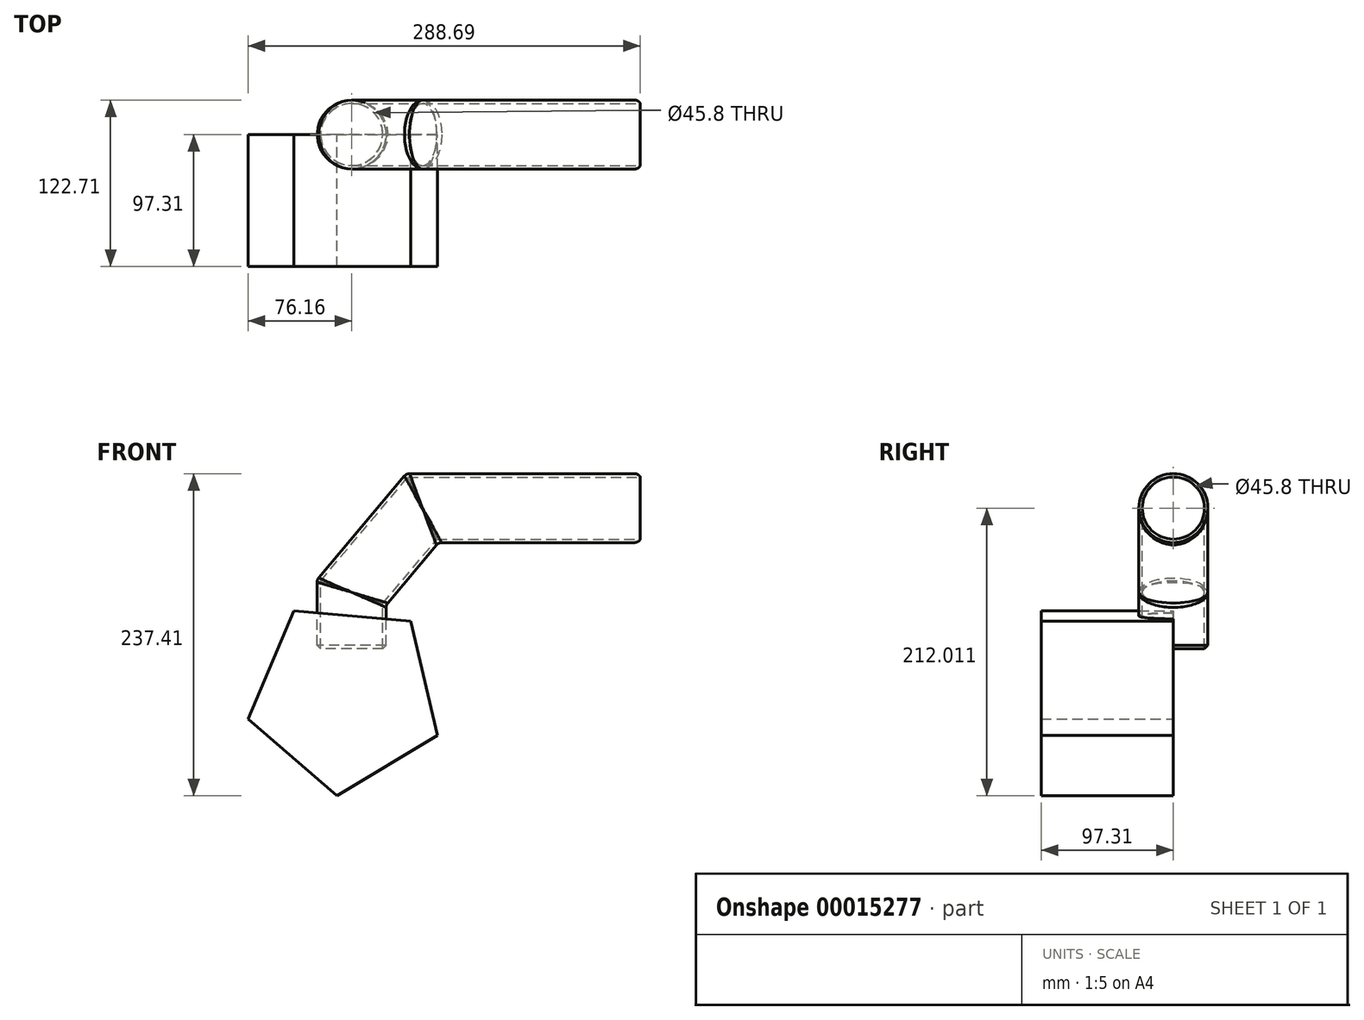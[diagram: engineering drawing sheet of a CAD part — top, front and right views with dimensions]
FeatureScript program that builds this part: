
annotation { "Feature Type Name" : "Feature", "Feature Type Description" : "" }
export const myFeature = defineFeature(function(context is Context, id is Id, definition is map)
    precondition{}
    {
        {
            var Q0;
            Q0=qCreatedBy(makeId("Top.planeOp"),FACE);
            var sketch = newSketch(context, id + "F0", { "sketchPlane" : qUnion([Q0])});
            skCircle(sketch, "E0", {"center": v(0, 0) * mm, "radius": 25.4 * mm});
            skSolve(sketch);
        }
        {
            var Q0;
            Q0=qCreatedBy(makeId("Front.planeOp"),FACE);
            var sketch = newSketch(context, id + "F1", { "sketchPlane" : qUnion([Q0])});
            skLineSegment(sketch, "E1", {"start": v(0, 0) * mm, "end": v(0, 44) * mm});
            skLineSegment(sketch, "E2", {"start": v(0, 44) * mm, "end": v(52.13, 106.03) * mm});
            skLineSegment(sketch, "E3", {"start": v(52.13, 106.03) * mm, "end": v(108.85, 106.03) * mm});
            skSolve(sketch);
        }
        {
            var Q0;
            Q0=makeQuery(id+"F0.imprint","IMPRINT",FACE,{"disambiguationData":[TD([[makeQuery(id+"F0.imprint","IMPRINT",EDGE,{"derivedFrom":sQuery(id+"F0.wireOp",EDGE,"E0")}),1.0]])]});
            var Q1;
            Q1=sQuery(id+"F1.wireOp",EDGE,"E1");
            var Q2;
            Q2=sQuery(id+"F1.wireOp",EDGE,"E2");
            var Q3;
            Q3=sQuery(id+"F1.wireOp",EDGE,"E3");
            sweep(context, id + "F2", {"profiles" : qUnion([Q0]), "path" : qUnion([Q1, Q2, Q3])});
        }
        {
            var Q0;
            Q0=makeQuery(id+"F2.opSweep","CAP_FACE",FACE,{"disambiguationData":[OSD([sQuery(id+"F0.wireOp",EDGE,"E0"),sQuery(id+"F1.wireOp",VERTEX,"E3.end")])],"isStart":false});
            var Q1;
            Q1=makeQuery(id+"F2.opSweep","CAP_FACE",FACE,{"disambiguationData":[OSD([sQuery(id+"F0.wireOp",EDGE,"E0"),sQuery(id+"F1.wireOp",VERTEX,"E1.start")])],"isStart":true});
            shell(context, id + "F3", {"entities" : qUnion([Q0, Q1]), "thickness" : 2.5 * mm});
        }
        {
            var Q0;
            Q0=makeQuery(id+"F2.opSweep","MID_CAP_EDGE",EDGE,{"disambiguationData":[OSD([sQuery(id+"F0.wireOp",EDGE,"E0"),sQuery(id+"F1.wireOp",VERTEX,"E3.start")])],"capPos":2.0});
            var Q1;
            Q1=makeQuery(id+"F2.opSweep","MID_CAP_EDGE",EDGE,{"disambiguationData":[OSD([sQuery(id+"F0.wireOp",EDGE,"E0"),sQuery(id+"F1.wireOp",VERTEX,"E2.start")])],"capPos":1.0});
            fillet(context, id + "F4", {"entities" : qUnion([Q0, Q1]), "radius" : 5 * mm, "tangentPropagation" : true, "allowEdgeOverflow" : false});
        }
        {
            var Q0;
            Q0=makeQuery(id+"F2.opSweep","CAP_EDGE",EDGE,{"disambiguationData":[OSD([sQuery(id+"F0.wireOp",EDGE,"E0"),sQuery(id+"F1.wireOp",VERTEX,"E1.start")])],"isStart":true});
            chamfer(context, id + "F5", {"entities" : qUnion([Q0]), "width" : 5 * mm, "tangentPropagation" : true});
        }
        {
            var Q0;
            Q0=makeQuery(id+"F2.opSweep","CAP_FACE",FACE,{"disambiguationData":[OSD([sQuery(id+"F0.wireOp",EDGE,"E0"),sQuery(id+"F1.wireOp",VERTEX,"E3.end")])],"isStart":false});
            extrude(context, id + "F6", {"entities" : qUnion([Q0]), "operationType" : NewBodyOperationType.ADD, "depth" : 103.68 * mm});
        }
        {
            var Q0;
            {var subQ0=sQuery(id+"F1.wireOp",VERTEX,"E3.end");var subQ1=sQuery(id+"F0.wireOp",EDGE,"E0");Q0=makeQuery(id+"F6.opExtrude","CAP_EDGE",EDGE,{"disambiguationData":[OSD([subQ1,subQ0]),TDD([makeQuery(id+"F2.opSweep","CAP_EDGE",EDGE,{"disambiguationData":[OSD([subQ1,subQ0])],"isStart":false})])],"isStart":false});}
            fillet(context, id + "F7", {"entities" : qUnion([Q0]), "radius" : 5 * mm, "tangentPropagation" : true, "allowEdgeOverflow" : false});
        }
        {
            var Q0;
            Q0=qCreatedBy(makeId("Front.planeOp"),FACE);
            var sketch = newSketch(context, id + "F8", { "sketchPlane" : qUnion([Q0])});
            skCircle(sketch, "E4.cCircle", {"center": v(-4.54, -32.72) * mm, "radius": 59.49 * mm, "construction": true});
            skLineSegment(sketch, "E4.0", {"start": v(43.64, 22.83) * mm, "end": v(63.18, -61.37) * mm});
            skLineSegment(sketch, "E4.1", {"start": v(63.18, -61.37) * mm, "end": v(-10.86, -105.98) * mm});
            skLineSegment(sketch, "E4.2", {"start": v(-10.86, -105.98) * mm, "end": v(-76.16, -49.34) * mm});
            skLineSegment(sketch, "E4.3", {"start": v(-76.16, -49.34) * mm, "end": v(-42.48, 30.26) * mm});
            skLineSegment(sketch, "E4.4", {"start": v(-42.48, 30.26) * mm, "end": v(43.64, 22.83) * mm});
            skPoint(sketch, "E4.0.midPoint", {"position": v(53.4, -19.27) * mm});
            skSolve(sketch);
        }
        {
            var Q0;
            Q0 = qSketchRegion(id + "F8", true);
            extrude(context, id + "F9", {"entities" : qUnion([Q0]), "operationType" : NewBodyOperationType.ADD, "depth" : 97.31 * mm});
        }
    });
